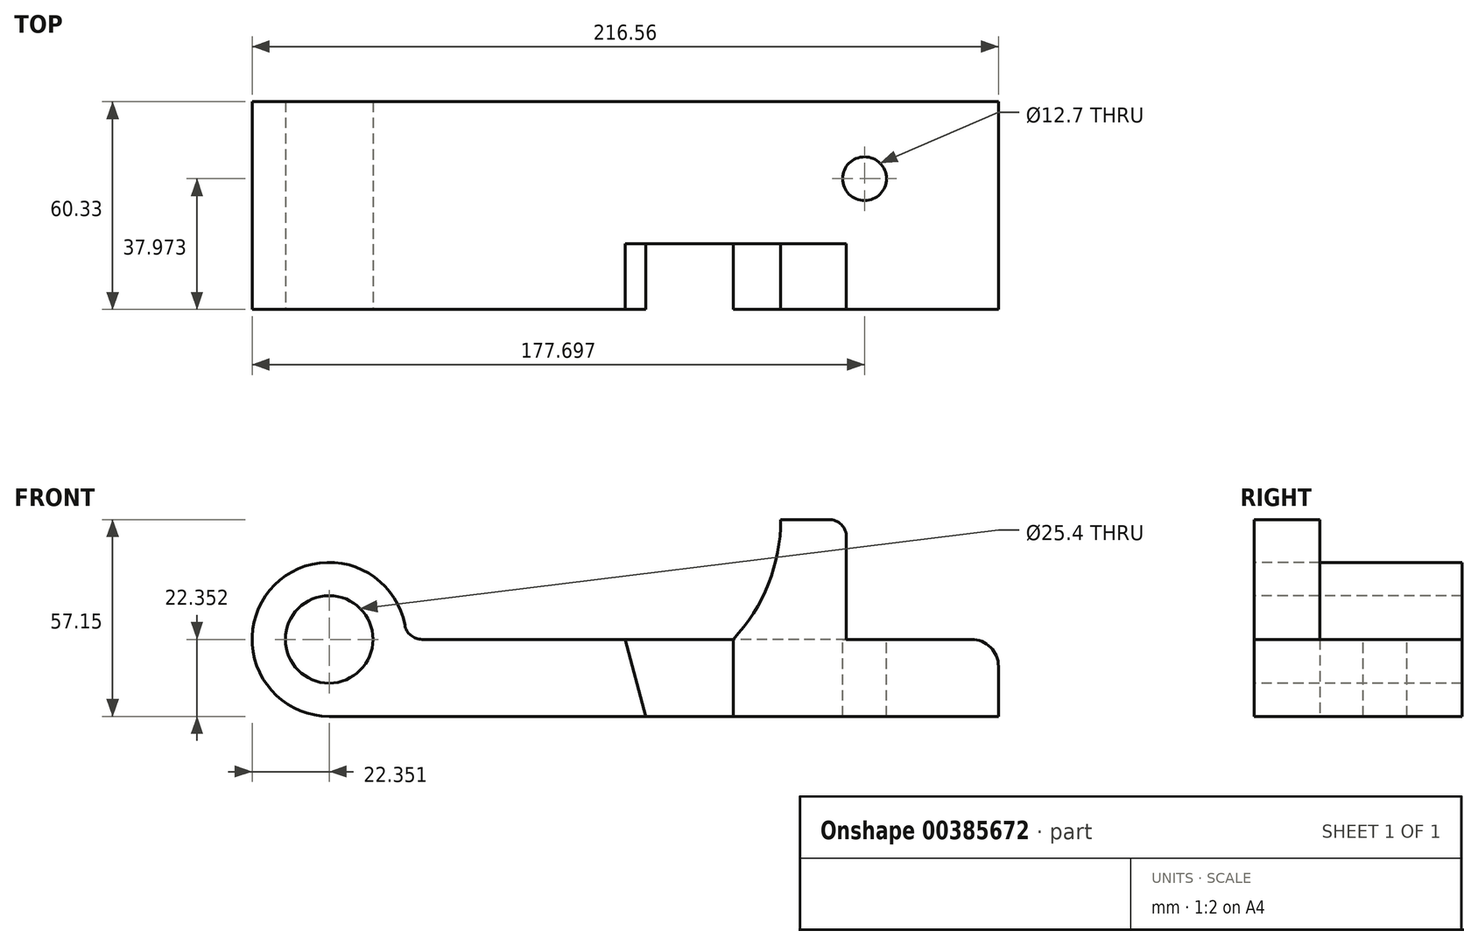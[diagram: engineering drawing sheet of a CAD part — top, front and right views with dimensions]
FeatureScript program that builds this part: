
annotation { "Feature Type Name" : "Feature", "Feature Type Description" : "" }
export const myFeature = defineFeature(function(context is Context, id is Id, definition is map)
    precondition{}
    {
        {
            var Q0;
            Q0=qCreatedBy(makeId("Front.planeOp"),FACE);
            var sketch = newSketch(context, id + "F0", { "sketchPlane" : qUnion([Q0])});
            skCircle(sketch, "E0", {"center": v(-55.1, 22.35) * mm, "radius": 22.35 * mm});
            skCircle(sketch, "E1", {"center": v(-55.1, 22.35) * mm, "radius": 12.7 * mm});
            skLineSegment(sketch, "E2", {"start": v(139.1, 0) * mm, "end": v(-55.1, 0) * mm});
            skLineSegment(sketch, "E3", {"start": v(139.1, 0) * mm, "end": v(139.1, 14.48) * mm});
            skLineSegment(sketch, "E4", {"start": v(131.23, 22.35) * mm, "end": v(-32.76, 22.35) * mm});
            skPoint(sketch, "E5.orphan", {"position": v(105.37, 0) * mm});
            skPoint(sketch, "E6.visualSharp", {"position": v(139.1, 22.35) * mm});
            skArc(sketch, "E6.filletArc", {"start": v(139.1, 14.48) * mm, "mid": v(136.8, 20.05) * mm, "end": v(131.23, 22.35) * mm});
            skLineSegment(sketch, "E7", {"start": v(30.74, 22.35) * mm, "end": v(36.74, 0) * mm});
            skLineSegment(sketch, "E8", {"start": v(62.14, 22.35) * mm, "end": v(62.14, 0) * mm});
            skLineSegment(sketch, "E9", {"start": v(94.98, 22.35) * mm, "end": v(94.98, 52.07) * mm});
            skLineSegment(sketch, "E10", {"start": v(89.9, 57.15) * mm, "end": v(75.93, 57.15) * mm});
            skArc(sketch, "E11", {"start": v(62.14, 22.35) * mm, "mid": v(72.36, 38.43) * mm, "end": v(75.93, 57.15) * mm});
            skPoint(sketch, "E12.visualSharp", {"position": v(94.98, 57.15) * mm});
            skArc(sketch, "E12.filletArc", {"start": v(94.98, 52.07) * mm, "mid": v(93.5, 55.66) * mm, "end": v(89.9, 57.15) * mm});
            skSolve(sketch);
        }
        {
            var Q0;
            Q0=makeQuery(id+"F0.imprint","IMPRINT",FACE,{"disambiguationData":[TD([[makeQuery(id+"F0.imprint","IMPRINT",EDGE,{"derivedFrom":sQuery(id+"F0.wireOp",EDGE,"E1")}),-1.0]])]});
            var Q1;
            {var subQ5=sQuery(id+"F0.wireOp",EDGE,"E7");Q1=makeQuery(id+"F0.imprint","IMPRINT",FACE,{"disambiguationData":[TD([[makeQuery(id+"F0.imprint","IMPRINT",EDGE,{"derivedFrom":subQ5}),-1.0]])]});}
            var Q2;
            {var subQ0=sQuery(id+"F0.wireOp",EDGE,"E7");Q2=makeQuery(id+"F0.imprint","IMPRINT",FACE,{"disambiguationData":[TD([[makeQuery(id+"F0.imprint","IMPRINT",EDGE,{"derivedFrom":subQ0}),1.0]])]});}
            var Q3;
            {var subQ3=sQuery(id+"F0.wireOp",EDGE,"E3");Q3=makeQuery(id+"F0.imprint","IMPRINT",FACE,{"disambiguationData":[TD([[makeQuery(id+"F0.imprint","IMPRINT",EDGE,{"derivedFrom":subQ3}),1.0]])]});}
            extrude(context, id + "F1", {"entities" : qUnion([Q0, Q1, Q2, Q3]), "oppositeDirection" : true, "depth" : 60.32 * mm});
        }
        {
            var Q0;
            {var subQ1=sQuery(id+"F0.wireOp",EDGE,"E9");Q0=makeQuery(id+"F0.imprint","IMPRINT",FACE,{"disambiguationData":[TD([[makeQuery(id+"F0.imprint","IMPRINT",EDGE,{"derivedFrom":subQ1}),1.0]])]});}
            extrude(context, id + "F2", {"entities" : qUnion([Q0]), "operationType" : NewBodyOperationType.ADD, "oppositeDirection" : true, "depth" : 19.05 * mm});
        }
        {
            var Q0;
            {var subQ0=sQuery(id+"F0.wireOp",EDGE,"E7");Q0=makeQuery(id+"F0.imprint","IMPRINT",FACE,{"disambiguationData":[TD([[makeQuery(id+"F0.imprint","IMPRINT",EDGE,{"derivedFrom":subQ0}),1.0]])]});}
            extrude(context, id + "F3", {"entities" : qUnion([Q0]), "operationType" : NewBodyOperationType.REMOVE, "oppositeDirection" : true, "depth" : 19.05 * mm});
        }
        {
            var Q0;
            Q0=makeQuery(id+"F1.opExtrude","SWEPT_EDGE",EDGE,{"disambiguationData":[OSD([sQuery(id+"F0.wireOp",EDGE,"E0"),sQuery(id+"F0.wireOp",EDGE,"E4")])]});
            var Q1;
            Q1=makeQuery(id+"F2.opExtrude","SWEPT_EDGE",EDGE,{"disambiguationData":[OSD([sQuery(id+"F0.wireOp",EDGE,"E4"),sQuery(id+"F0.wireOp",EDGE,"E9")])]});
            fillet(context, id + "F4", {"entities" : qUnion([Q0, Q1]), "radius" : 5.08 * mm, "tangentPropagation" : true, "allowEdgeOverflow" : false});
        }
        {
            var Q0;
            Q0=makeQuery(id+"F1.opExtrude","SWEPT_FACE",FACE,{"disambiguationData":[OSD([sQuery(id+"F0.wireOp",EDGE,"E4")])]});
            var sketch = newSketch(context, id + "F5", { "sketchPlane" : qUnion([Q0])});
            skLineSegment(sketch, "E13.0", {"start": v(131.23, 60.33) * mm, "end": v(-28.15, 60.33) * mm});
            skLineSegment(sketch, "E14.0", {"start": v(139.1, 60.33) * mm, "end": v(139.1, 0) * mm});
            skCircle(sketch, "E15", {"center": v(100.24, 37.97) * mm, "radius": 6.35 * mm});
            skSolve(sketch);
        }
        {
            var Q0;
            Q0=makeQuery(id+"F5.imprint","IMPRINT",FACE,{"disambiguationData":[TD([[makeQuery(id+"F5.imprint","IMPRINT",EDGE,{"derivedFrom":sQuery(id+"F5.wireOp",EDGE,"E15")}),1.0]])]});
            extrude(context, id + "F6", {"entities" : qUnion([Q0]), "operationType" : NewBodyOperationType.REMOVE, "oppositeDirection" : true, "depth" : 25.4 * mm});
        }
    });
